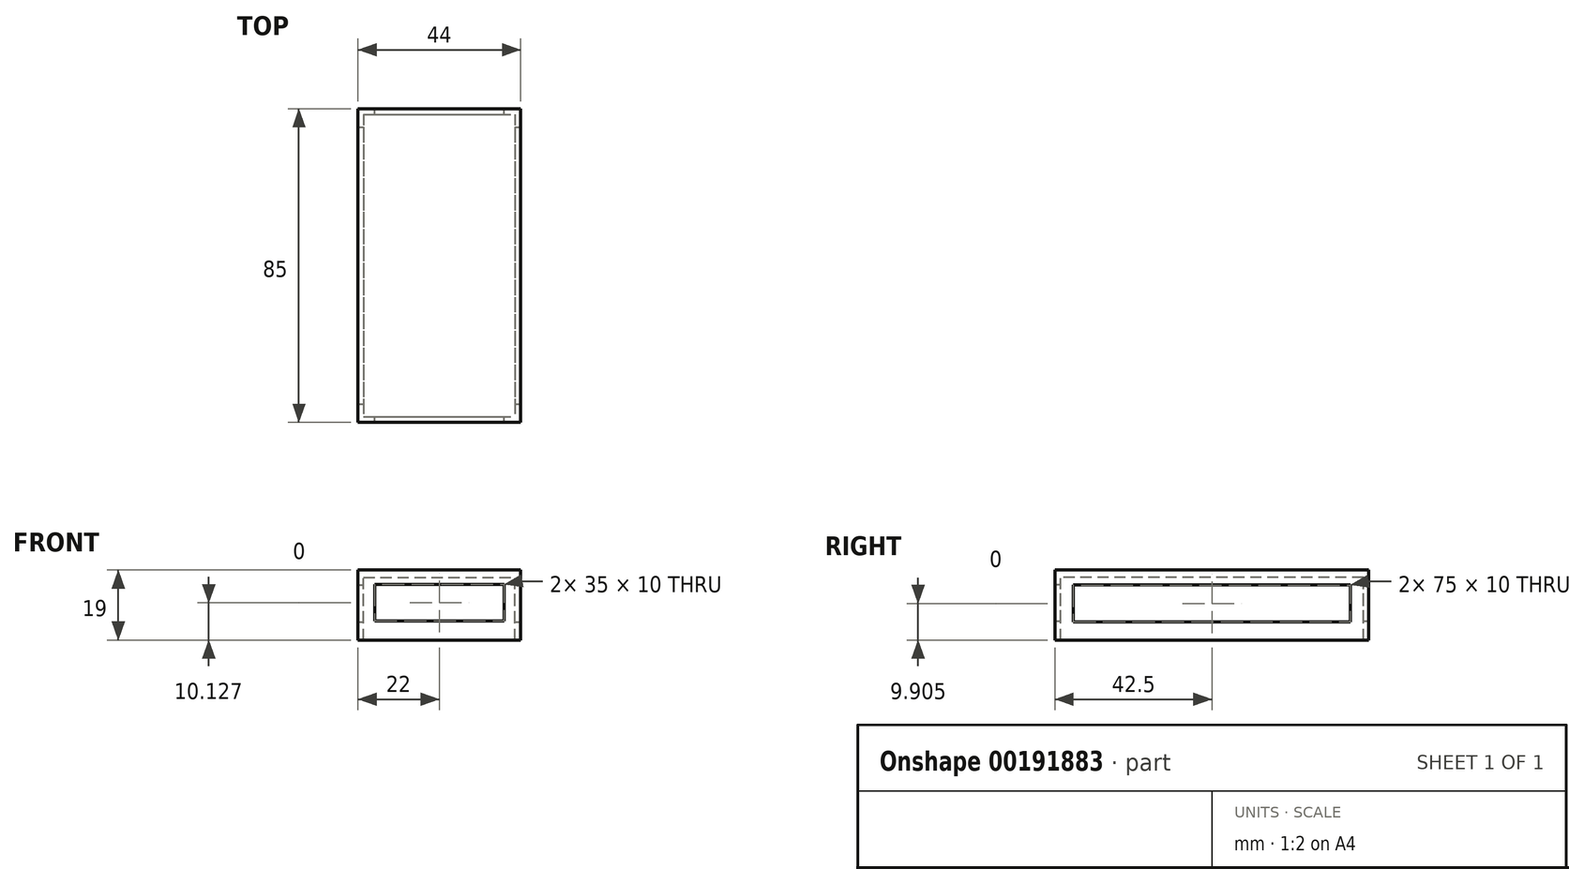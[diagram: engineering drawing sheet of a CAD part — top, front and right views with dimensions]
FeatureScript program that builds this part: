
annotation { "Feature Type Name" : "Feature", "Feature Type Description" : "" }
export const myFeature = defineFeature(function(context is Context, id is Id, definition is map)
    precondition{}
    {
        {
            var Q0;
            Q0=qCreatedBy(makeId("Top.planeOp"),FACE);
            var sketch = newSketch(context, id + "F0", { "sketchPlane" : qUnion([Q0])});
            skLineSegment(sketch, "E0.bottom", {"start": v(22, -42.5) * mm, "end": v(-22, -42.5) * mm});
            skLineSegment(sketch, "E0.top", {"start": v(22, 42.5) * mm, "end": v(-22, 42.5) * mm});
            skLineSegment(sketch, "E0.left", {"start": v(22, -42.5) * mm, "end": v(22, 42.5) * mm});
            skLineSegment(sketch, "E0.right", {"start": v(-22, -42.5) * mm, "end": v(-22, 42.5) * mm});
            skPoint(sketch, "E0.middle", {"position": v(0, 0) * mm});
            skLineSegment(sketch, "E1.0", {"start": v(-20.5, -41) * mm, "end": v(-20.5, 41) * mm});
            skLineSegment(sketch, "E1.1", {"start": v(20.5, -41) * mm, "end": v(-20.5, -41) * mm});
            skLineSegment(sketch, "E1.2", {"start": v(20.5, -41) * mm, "end": v(20.5, 41) * mm});
            skLineSegment(sketch, "E1.3", {"start": v(20.5, 41) * mm, "end": v(-20.5, 41) * mm});
            skSolve(sketch);
        }
        {
            var Q0;
            Q0=makeQuery(id+"F0.imprint","IMPRINT",FACE,{"disambiguationData":[TD([[makeQuery(id+"F0.imprint","IMPRINT",EDGE,{"derivedFrom":sQuery(id+"F0.wireOp",EDGE,"E0.bottom")}),-1.0]])]});
            extrude(context, id + "F1", {"entities" : qUnion([Q0]), "oppositeDirection" : true, "depth" : 19 * mm});
        }
        {
            var Q0;
            Q0=makeQuery(id+"F0.imprint","IMPRINT",FACE,{"disambiguationData":[TD([[makeQuery(id+"F0.imprint","IMPRINT",EDGE,{"derivedFrom":sQuery(id+"F0.wireOp",EDGE,"E1.0")}),-1.0]])]});
            var sketch = newSketch(context, id + "F2", { "sketchPlane" : qUnion([Q0])});
            skLineSegment(sketch, "E2.bottom", {"start": v(20.5, 41.5) * mm, "end": v(-20.5, 41.5) * mm});
            skLineSegment(sketch, "E2.top", {"start": v(20.5, -41.5) * mm, "end": v(-20.5, -41.5) * mm});
            skLineSegment(sketch, "E2.left", {"start": v(20.5, 41.5) * mm, "end": v(20.5, -41.5) * mm});
            skLineSegment(sketch, "E2.right", {"start": v(-20.5, 41.5) * mm, "end": v(-20.5, -41.5) * mm});
            skPoint(sketch, "E2.middle", {"position": v(0, 0) * mm});
            skSolve(sketch);
        }
        {
            var Q0;
            Q0 = qSketchRegion(id + "F2", true);
            extrude(context, id + "F3", {"entities" : qUnion([Q0]), "operationType" : NewBodyOperationType.ADD, "oppositeDirection" : true, "depth" : 2 * mm});
        }
        {
            var Q0;
            Q0=makeQuery(id+"F1.opExtrude","SWEPT_FACE",FACE,{"disambiguationData":[OSD([sQuery(id+"F0.wireOp",EDGE,"E0.left")])]});
            var sketch = newSketch(context, id + "F4", { "sketchPlane" : qUnion([Q0])});
            skLineSegment(sketch, "E3.bottom", {"start": v(37.5, -14.1) * mm, "end": v(-37.5, -14.1) * mm});
            skLineSegment(sketch, "E3.top", {"start": v(37.5, -4.1) * mm, "end": v(-37.5, -4.1) * mm});
            skLineSegment(sketch, "E3.left", {"start": v(37.5, -14.1) * mm, "end": v(37.5, -4.1) * mm});
            skLineSegment(sketch, "E3.right", {"start": v(-37.5, -14.1) * mm, "end": v(-37.5, -4.1) * mm});
            skPoint(sketch, "E3.middle", {"position": v(0, -9.1) * mm});
            skSolve(sketch);
        }
        {
            var Q0;
            Q0=makeQuery(id+"F4.imprint","IMPRINT",FACE,{"disambiguationData":[TD([[makeQuery(id+"F4.imprint","IMPRINT",EDGE,{"derivedFrom":sQuery(id+"F4.wireOp",EDGE,"E3.bottom")}),-1.0]])]});
            extrude(context, id + "F5", {"entities" : qUnion([Q0]), "operationType" : NewBodyOperationType.REMOVE, "endBound" : BoundingType.THROUGH_ALL, "oppositeDirection" : true, "depth" : 25 * mm});
        }
        {
            var Q0;
            Q0=makeQuery(id+"F1.opExtrude","SWEPT_FACE",FACE,{"disambiguationData":[OSD([sQuery(id+"F0.wireOp",EDGE,"E0.top")])]});
            var sketch = newSketch(context, id + "F6", { "sketchPlane" : qUnion([Q0])});
            skLineSegment(sketch, "E4.bottom", {"start": v(17.5, -13.87) * mm, "end": v(-17.5, -13.87) * mm});
            skLineSegment(sketch, "E4.top", {"start": v(17.5, -3.87) * mm, "end": v(-17.5, -3.87) * mm});
            skLineSegment(sketch, "E4.left", {"start": v(17.5, -13.87) * mm, "end": v(17.5, -3.87) * mm});
            skLineSegment(sketch, "E4.right", {"start": v(-17.5, -13.87) * mm, "end": v(-17.5, -3.87) * mm});
            skPoint(sketch, "E4.middle", {"position": v(0, -8.87) * mm});
            skSolve(sketch);
        }
        {
            var Q0;
            Q0=makeQuery(id+"F6.imprint","IMPRINT",FACE,{"disambiguationData":[TD([[makeQuery(id+"F6.imprint","IMPRINT",EDGE,{"derivedFrom":sQuery(id+"F6.wireOp",EDGE,"E4.bottom")}),-1.0]])]});
            extrude(context, id + "F7", {"entities" : qUnion([Q0]), "operationType" : NewBodyOperationType.REMOVE, "endBound" : BoundingType.THROUGH_ALL, "oppositeDirection" : true, "depth" : 25 * mm});
        }
    });
